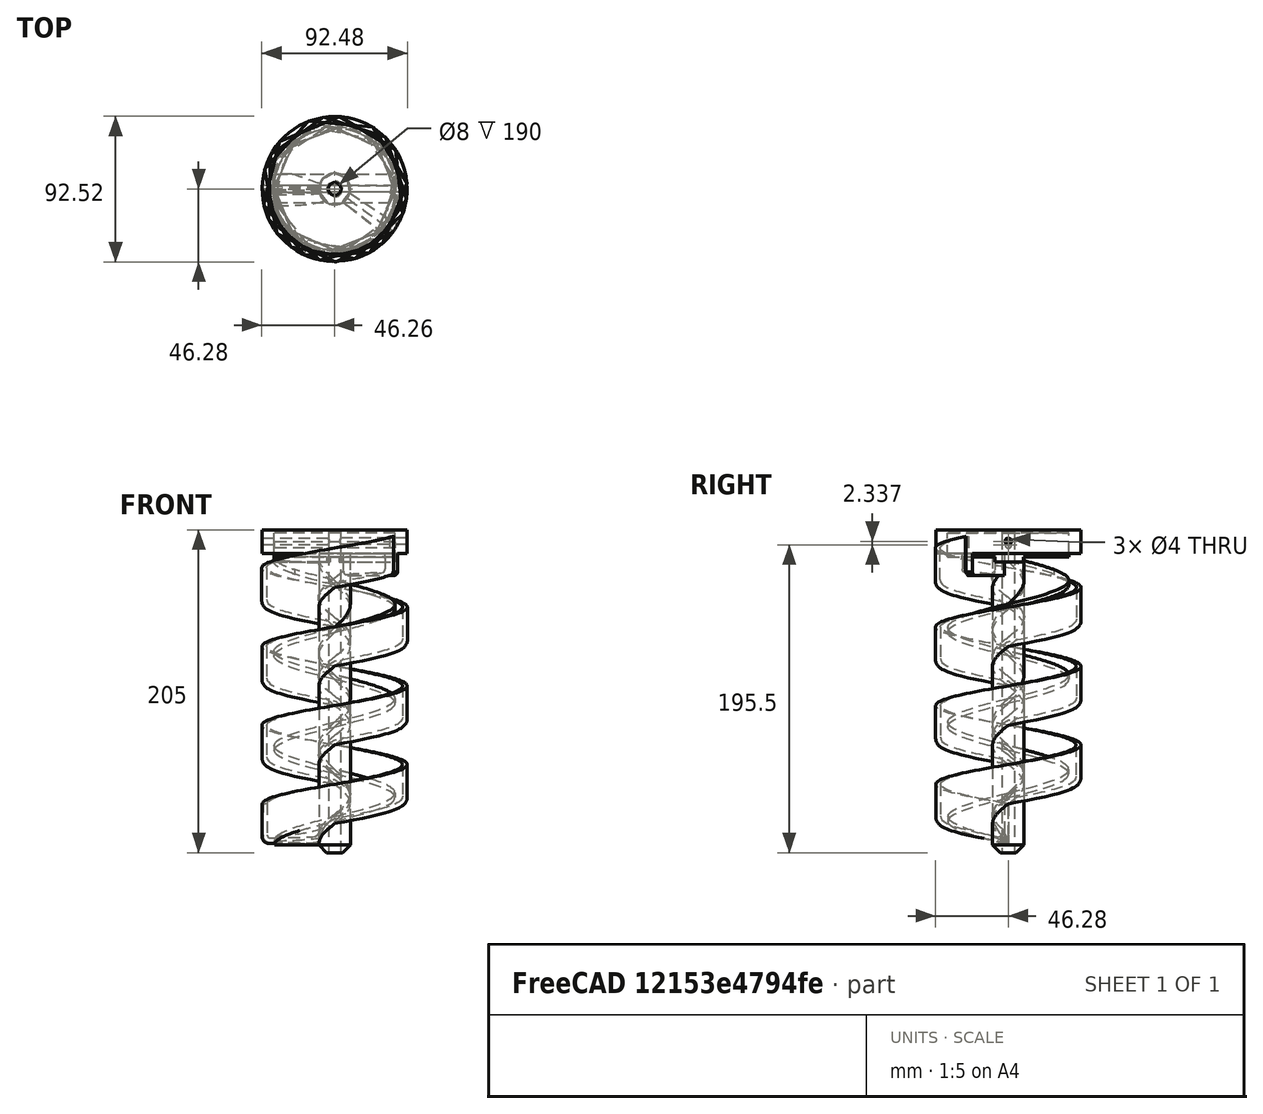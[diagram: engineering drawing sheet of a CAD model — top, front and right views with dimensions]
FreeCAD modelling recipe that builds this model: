
FCSTD DOCUMENT  (FreeCAD 1.1R14555 (Git shallow))
Label: Body - 1.2
License: All rights reserved
LicenseURL: https://en.wikipedia.org/wiki/All_rights_reserved
objects: Sketcher::SketchObject×14, PartDesign::Pad×8, PartDesign::Pocket×7, PartDesign::Chamfer×6, PartDesign::AdditiveHelix×2, PartDesign::Body×2, App::Point×2, PartDesign::Fillet×1
note: 102 computed .brp shape members not serialized (recipe doc carries the construction recipe); baked Part::Feature solids carry a one-line shape summary decoded from their .brp

FEATURE [Sketcher::SketchObject] Sketch
  ArcFitTolerance = 1e-06
  AttachmentSupport = -> [XY_Plane]
  ExternalTypes = [0]
  FullyConstrained = true
  MakeInternals = false
  MapMode = 5
  sketch-geometry (1):
    g0: Circle CenterX=0 CenterY=0 CenterZ=0 NormalX=0 NormalY=0 NormalZ=1 AngleXU=0 Radius=10
  constraints (2):
    c: Coincident(g0,g-1)
    c: Diameter(g0) = 20
FEATURE [PartDesign::Pad] Pad
  Direction = (0,0,1)
  Length = 200
  Length2 = 10
  Profile = -> Sketch
  ReferenceAxis = -> Sketch [N_Axis]
  Refine = true
  SideType = 0
  Suppressed = false
  Type = 0
  Type2 = 0
FEATURE [PartDesign::Chamfer] Chamfer
  Angle = 45
  Base = -> Pad [Edge2]
  BaseFeature = -> Pad
  ChamferType = 0
  FlipDirection = false
  Refine = true
  Size = 5
  Size2 = 1
  SupportTransform = false
  Suppressed = false
  UseAllEdges = false
FEATURE [Sketcher::SketchObject] Sketch001
  ArcFitTolerance = 1e-06
  AttachmentSupport = -> [XZ_Plane]
  ExternalGeometry = -> [Chamfer]
  ExternalTypes = [0]
  FullyConstrained = true
  MakeInternals = false
  MapMode = 5
  Placement = pos=(0,0,0) rot=(1,0,0;1.5708rad)
  expr: Constraints[11] = 77 / 2 - 0.3
  sketch-geometry (4):
    g0: LineSegment StartX=-38.2 StartY=8 StartZ=0 EndX=-38.2 EndY=5 EndZ=0
    g1: LineSegment StartX=-38.2 StartY=5 StartZ=0 EndX=0 EndY=5 EndZ=0
    g2: LineSegment StartX=0 StartY=5 StartZ=0 EndX=0 EndY=8 EndZ=0
    g3: LineSegment StartX=0 StartY=8 StartZ=0 EndX=-38.2 EndY=8 EndZ=0
  constraints (12):
    c: Coincident(g0,g1)
    c: Coincident(g1,g2)
    c: Coincident(g2,g3)
    c: Coincident(g3,g0)
    c: Vertical(g0)
    c: Vertical(g2)
    c: Horizontal(g1)
    c: Horizontal(g3)
    c: PointOnObject(g1,g-2)
    c: Horizontal(g0,g-3)
    c: DistanceY(g0,g0) = 3
    c: DistanceX(g1,g1) = 38.2
FEATURE [PartDesign::AdditiveHelix] AdditiveHelix
  Angle = 0.1
  Axis = (0,2e-16,1)
  Base = (0,0,0)
  BaseFeature = -> Chamfer
  Growth = 0.10472
  HasBeenEdited = true
  Height = 180
  LeftHanded = false
  Mode = 0
  Outside = false
  Pitch = 60
  Profile = -> Sketch001
  ReferenceAxis = -> Sketch001 [V_Axis]
  Refine = true
  Suppressed = false
  Tolerance = 0.1
  Turns = 3
FEATURE [Sketcher::SketchObject] Sketch002
  ArcFitTolerance = 1e-06
  AttachmentSupport = -> [Chamfer]
  ExternalTypes = [0]
  FullyConstrained = true
  MakeInternals = false
  MapMode = 5
  Placement = pos=(0,0,200) rot=(0,0,1;0rad)
  sketch-geometry (1):
    g0: Circle CenterX=0 CenterY=0 CenterZ=0 NormalX=0 NormalY=0 NormalZ=1 AngleXU=0 Radius=38.5
  constraints (2):
    c: Coincident(g0,g-1)
    c: Diameter(g0) = 77
FEATURE [PartDesign::Chamfer] Chamfer001
  Angle = 45
  Base = -> AdditiveHelix [Edge12]
  BaseFeature = -> AdditiveHelix
  ChamferType = 0
  FlipDirection = false
  Refine = true
  Size = 2.99
  Size2 = 1
  SupportTransform = false
  Suppressed = false
  UseAllEdges = false
FEATURE [PartDesign::Chamfer] Chamfer002
  Angle = 45
  Base = -> Chamfer001 [Edge12]
  BaseFeature = -> Chamfer001
  ChamferType = 0
  FlipDirection = false
  Refine = true
  Size = 4
  Size2 = 1
  SupportTransform = false
  Suppressed = false
  UseAllEdges = false
FEATURE [PartDesign::Chamfer] Chamfer003
  Angle = 45
  Base = -> Chamfer002 [Edge13]
  BaseFeature = -> Chamfer002
  ChamferType = 0
  FlipDirection = false
  Refine = true
  Size = 4
  Size2 = 1
  SupportTransform = false
  Suppressed = false
  UseAllEdges = false
FEATURE [PartDesign::Pad] Pad001
  BaseFeature = -> Chamfer003
  Direction = (0,0,1)
  Length = 3
  Length2 = 10
  Profile = -> Sketch002
  ReferenceAxis = -> Sketch002 [N_Axis]
  Refine = true
  SideType = 0
  Suppressed = false
  Type = 0
  Type2 = 0
FEATURE [Sketcher::SketchObject] Sketch003
  ArcFitTolerance = 1e-06
  AttachmentSupport = -> [Pad001]
  ExternalTypes = [0]
  FullyConstrained = true
  MakeInternals = false
  MapMode = 5
  Placement = pos=(0,0,200) rot=(1,0,0;3.14159rad)
  sketch-geometry (1):
    g0: Circle CenterX=0 CenterY=0 CenterZ=0 NormalX=0 NormalY=0 NormalZ=1 AngleXU=0 Radius=38.5
  constraints (2):
    c: Coincident(g0,g-1)
    c: Diameter(g0) = 77
FEATURE [PartDesign::Pad] Pad002
  BaseFeature = -> Pad001
  Direction = (0,0,-1)
  Length = 12
  Length2 = 10
  Profile = -> Sketch003
  ReferenceAxis = -> Sketch003 [N_Axis]
  Refine = true
  SideType = 0
  Suppressed = false
  Type = 0
  Type2 = 0
FEATURE [PartDesign::Fillet] Fillet
  Base = -> Pad002 [Edge36]
  BaseFeature = -> Pad002
  Radius = 3
  Refine = true
  SupportTransform = false
  Suppressed = false
  UseAllEdges = false
FEATURE [Sketcher::SketchObject] Sketch004
  ArcFitTolerance = 1e-06
  AttachmentSupport = -> [Fillet]
  ExternalTypes = [0]
  FullyConstrained = true
  MakeInternals = false
  MapMode = 5
  Placement = pos=(0,0,203) rot=(0,0,1;0rad)
  sketch-geometry (2):
    g0: Circle CenterX=0 CenterY=0 CenterZ=0 NormalX=0 NormalY=0 NormalZ=1 AngleXU=0 Radius=38.5
    g1: Circle CenterX=0 CenterY=0 CenterZ=0 NormalX=0 NormalY=0 NormalZ=1 AngleXU=0 Radius=50
  constraints (4):
    c: Coincident(g0,g-1)
    c: Diameter(g0) = 77
    c: Coincident(g1,g0)
    c: Diameter(g1) = 100
FEATURE [PartDesign::Pocket] Pocket
  BaseFeature = -> Fillet
  Direction = (0,0,-1)
  Length = 180
  Length2 = 5
  Profile = -> Sketch004
  ReferenceAxis = -> Sketch004 [N_Axis]
  Refine = true
  Reversed = true
  SideType = 0
  Suppressed = false
  Type = 0
  Type2 = 0
FEATURE [Sketcher::SketchObject] Sketch005
  ArcFitTolerance = 1e-06
  AttachmentSupport = -> [YZ_Plane]
  ExternalGeometry = -> [Pocket]
  ExternalTypes = [0]
  FullyConstrained = true
  MakeInternals = false
  MapMode = 5
  Placement = pos=(0,0,0) rot=(0.57735,0.57735,0.57735;2.0944rad)
  sketch-geometry (1):
    g0: Circle CenterX=9.4e-15 CenterY=195.5 CenterZ=0 NormalX=0 NormalY=0 NormalZ=1 AngleXU=0 Radius=2
  constraints (3):
    c: PointOnObject(g0,g-3)
    c: Diameter(g0) = 4
    c: Symmetric(g-3,g-3,g0)
FEATURE [PartDesign::Pocket] Pocket001
  BaseFeature = -> Pocket
  Direction = (-1,0,0)
  Length = 500
  Length2 = 5
  Profile = -> Sketch005
  ReferenceAxis = -> Sketch005 [N_Axis]
  Refine = true
  Reversed = true
  SideType = 0
  Suppressed = false
  Type = 0
  Type2 = 0
FEATURE [PartDesign::Pocket] Pocket002
  BaseFeature = -> Pocket001
  Direction = (-1,0,0)
  Length = 5
  Length2 = 5
  Profile = -> Pocket001 [Face21]
  Refine = true
  SideType = 0
  Suppressed = false
  Type = 1
  Type2 = 0
FEATURE [Sketcher::SketchObject] Sketch006
  ArcFitTolerance = 1e-06
  AttachmentSupport = -> [YZ_Plane]
  ExternalTypes = [0]
  FullyConstrained = false
  MakeInternals = false
  MapMode = 5
  Placement = pos=(0,0,0) rot=(0.57735,0.57735,0.57735;2.0944rad)
  sketch-geometry (4):
    g0: LineSegment StartX=9.56195 StartY=192.563 StartZ=0 EndX=-8.62475 EndY=192.563 EndZ=0
    g1: LineSegment StartX=-8.62475 StartY=192.563 StartZ=0 EndX=-8.62475 EndY=184.759 EndZ=0
    g2: LineSegment StartX=-8.62475 StartY=184.759 StartZ=0 EndX=9.56195 EndY=184.759 EndZ=0
    g3: LineSegment StartX=9.56195 StartY=184.759 StartZ=0 EndX=9.56195 EndY=192.563 EndZ=0
  constraints (8):
    c: Coincident(g0,g1)
    c: Coincident(g1,g2)
    c: Coincident(g2,g3)
    c: Coincident(g3,g0)
    c: Horizontal(g0)
    c: Horizontal(g2)
    c: Vertical(g1)
    c: Vertical(g3)
FEATURE [PartDesign::Pad] Pad003
  BaseFeature = -> Pocket002
  Direction = (1,0,0)
  Length = 50
  Length2 = 50
  Profile = -> Sketch006
  ReferenceAxis = -> Sketch006 [N_Axis]
  Refine = true
  SideType = 0
  Suppressed = false
  Type = 4
  Type2 = 0
FEATURE [Sketcher::SketchObject] Sketch007
  ArcFitTolerance = 1e-06
  AttachmentSupport = -> [Pad003]
  ExternalTypes = [0]
  FullyConstrained = true
  MakeInternals = false
  MapMode = 5
  Placement = pos=(0,0,203) rot=(0,0,1;0rad)
  sketch-geometry (2):
    g0: Circle CenterX=0 CenterY=0 CenterZ=0 NormalX=0 NormalY=0 NormalZ=1 AngleXU=0 Radius=38.5
    g1: Circle CenterX=0 CenterY=0 CenterZ=0 NormalX=0 NormalY=0 NormalZ=1 AngleXU=0 Radius=55
  constraints (4):
    c: Coincident(g0,g-1)
    c: Diameter(g0) = 77
    c: Diameter(g1) = 110
    c: Coincident(g1,g0)
FEATURE [PartDesign::Pocket] Pocket003
  BaseFeature = -> Pad003
  Direction = (0,0,-1)
  Length = 30
  Length2 = 5
  Profile = -> Sketch007
  ReferenceAxis = -> Sketch007 [N_Axis]
  Refine = true
  SideType = 0
  Suppressed = false
  Type = 0
  Type2 = 0
FEATURE [PartDesign::Body] Body
  AllowCompound = false
  Group = -> [Sketch,Pad,Chamfer,Sketch001,AdditiveHelix,Sketch002,Chamfer001,Chamfer002,Chamfer003,Pad001,Sketch003,Pad002,Fillet,Sketch004,Pocket,Sketch005,Pocket001,Pocket002,Sketch006,Pad003,Sketch007,Pocket003]
  Origin = -> Origin
  Tip = -> Pocket003
FEATURE [Sketcher::SketchObject] Sketch008
  ArcFitTolerance = 1e-06
  AttachmentSupport = -> [XY_Plane001]
  ExternalTypes = [0]
  FullyConstrained = true
  MakeInternals = false
  MapMode = 5
  sketch-geometry (2):
    g0: Circle CenterX=0 CenterY=0 CenterZ=0 NormalX=0 NormalY=0 NormalZ=1 AngleXU=0 Radius=10
    g1: Circle CenterX=0 CenterY=0 CenterZ=0 NormalX=0 NormalY=0 NormalZ=1 AngleXU=0 Radius=4
  constraints (4):
    c: Coincident(g0,g-1)
    c: Diameter(g0) = 20
    c: Coincident(g1,g0)
    c: Diameter(g1) = 8
FEATURE [PartDesign::Pad] Pad004
  Direction = (0,0,1)
  Length = 200
  Length2 = 10
  Profile = -> Sketch008
  ReferenceAxis = -> Sketch008 [N_Axis]
  Refine = true
  SideType = 0
  Suppressed = false
  Type = 0
  Type2 = 0
FEATURE [PartDesign::Chamfer] Chamfer004
  Angle = 45
  Base = -> Pad004 [Edge2]
  BaseFeature = -> Pad004
  ChamferType = 0
  FlipDirection = false
  Refine = true
  Size = 5
  Size2 = 1
  SupportTransform = false
  Suppressed = false
  UseAllEdges = false
FEATURE [Sketcher::SketchObject] Sketch009
  ArcFitTolerance = 1e-06
  AttachmentSupport = -> [XZ_Plane001]
  ExternalGeometry = -> [Chamfer004]
  ExternalTypes = [0]
  FullyConstrained = true
  MakeInternals = false
  MapMode = 5
  Placement = pos=(0,0,0) rot=(1,0,0;1.5708rad)
  sketch-geometry (12):
    g0: LineSegment StartX=-42 StartY=6 StartZ=0 EndX=-10 EndY=6 EndZ=0
    g1: LineSegment StartX=-13 StartY=9 StartZ=0 EndX=-41 EndY=9 EndZ=0
    g2: LineSegment StartX=-46 StartY=10 StartZ=0 EndX=-46 EndY=31 EndZ=0
    g3: LineSegment StartX=-43 StartY=31 StartZ=0 EndX=-43 EndY=11 EndZ=0
    g4: ArcOfCircle CenterX=-41 CenterY=11 CenterZ=0 NormalX=0 NormalY=0 NormalZ=1 AngleXU=0 Radius=2 StartAngle=3.14159 EndAngle=4.71239
    g5: GeomPoint [constr] X=-43 Y=9 Z=0
    g6: ArcOfCircle CenterX=-42 CenterY=10 CenterZ=0 NormalX=0 NormalY=0 NormalZ=1 AngleXU=0 Radius=4 StartAngle=3.14159 EndAngle=4.71239
    g7: ArcOfCircle CenterX=-13 CenterY=12 CenterZ=0 NormalX=0 NormalY=0 NormalZ=1 AngleXU=0 Radius=3 StartAngle=4.71239 EndAngle=6.28319
    g8: LineSegment StartX=-10 StartY=12 StartZ=0 EndX=-8 EndY=12 EndZ=0
    g9: LineSegment StartX=-10 StartY=6 StartZ=0 EndX=-8 EndY=6 EndZ=0
    g10: LineSegment StartX=-8 StartY=12 StartZ=0 EndX=-8 EndY=6 EndZ=0
    g11: LineSegment StartX=-46 StartY=31 StartZ=0 EndX=-43 EndY=31 EndZ=0
  constraints (34):
    c: Vertical(g2)
    c: Vertical(g3)
    c: PointOnObject(g5,g1)
    c: PointOnObject(g5,g3)
    c: Tangent(g1,g4) = 1.5708
    c: Tangent(g3,g4) = -1.5708
    c: Tangent(g0,g6) = -1.5708
    c: Tangent(g2,g6) = 1.5708
    c: DistanceY(g3,g3) = 20
    c: Radius(g4) = 2
    c: Radius(g6) = 4
    c: Horizontal(g1)
    c: Horizontal(g0)
    c: Vertical(g0,g-3)
    c: DistanceX(g2,g-1) = 46
    c: DistanceY(g-1,g0) = 6
    c: Coincident(g7,g1)
    c: Vertical(g7,g1)
    c: Radius(g7) = 3
    c: Vertical(g7,g0)
    c: Horizontal(g7,g7)
    c: DistanceY(g0,g1) = 3
    c: Coincident(g8,g7)
    c: Coincident(g9,g0)
    c: Horizontal(g9)
    c: Coincident(g10,g8)
    c: Coincident(g10,g9)
    c: Vertical(g10)
    c: Horizontal(g8)
    c: Distance(g8,g8) = 2
    c: Horizontal(g2,g3)
    c: DistanceX(g2,g3) = 3
    c: Coincident(g11,g2)
    c: Coincident(g11,g3)
FEATURE [PartDesign::AdditiveHelix] AdditiveHelix001
  Angle = 0.1
  Axis = (0,2e-16,1)
  Base = (0,0,0)
  BaseFeature = -> Chamfer004
  Growth = 0.0872666
  HasBeenEdited = true
  Height = 170
  LeftHanded = false
  Mode = 0
  Outside = false
  Pitch = 50
  Profile = -> Sketch009
  ReferenceAxis = -> Sketch009 [V_Axis]
  Refine = true
  Suppressed = false
  Tolerance = 0.1
  Turns = 3.4
FEATURE [App::Point] Origin002  label="Origin"
  Role = Origin
FEATURE [App::Point] Origin003  label="Origin"
  Role = Origin
FEATURE [Sketcher::SketchObject] Sketch010
  ArcFitTolerance = 1e-06
  AttachmentSupport = -> [AdditiveHelix001]
  ExternalTypes = [0]
  FullyConstrained = true
  MakeInternals = false
  MapMode = 5
  Placement = pos=(0,0,200) rot=(0,0,1;0rad)
  expr: Constraints[3] = 46 * 2
  sketch-geometry (2):
    g0: Circle CenterX=0 CenterY=0 CenterZ=0 NormalX=0 NormalY=0 NormalZ=1 AngleXU=0 Radius=4
    g1: Circle CenterX=0 CenterY=0 CenterZ=0 NormalX=0 NormalY=0 NormalZ=1 AngleXU=0 Radius=46
  constraints (4):
    c: Diameter(g0) = 8
    c: Coincident(g0,g-1)
    c: Coincident(g1,g0)
    c: Diameter(g1) = 92
FEATURE [PartDesign::Pad] Pad005
  BaseFeature = -> AdditiveHelix001
  Direction = (0,0,1)
  Length = 5
  Length2 = 10
  Profile = -> Sketch010
  ReferenceAxis = -> Sketch010 [N_Axis]
  SideType = 1
  Suppressed = false
  Type = 0
  Type2 = 0
FEATURE [Sketcher::SketchObject] Sketch011
  ArcFitTolerance = 1e-06
  AttachmentSupport = -> [Pad005]
  ExternalTypes = [0]
  FullyConstrained = false
  MakeInternals = false
  MapMode = 5
  Placement = pos=(0,0,205) rot=(0,0,1;0rad)
  sketch-geometry (4):
    g0: LineSegment StartX=3.72918 StartY=1.44679 StartZ=0 EndX=40.0304 EndY=-22.662 EndZ=0
    g1: LineSegment StartX=34.1872 StartY=-30.7772 StartZ=0 EndX=-0.528085 EndY=-3.96499 EndZ=0
    g2: ArcOfCircle CenterX=0 CenterY=0 CenterZ=0 NormalX=0 NormalY=0 NormalZ=1 AngleXU=0 Radius=46 StartAngle=5.55023 EndAngle=5.76805
    g3: ArcOfCircle CenterX=0 CenterY=0 CenterZ=0 NormalX=0 NormalY=0 NormalZ=1 AngleXU=0 Radius=4 StartAngle=4.57998 EndAngle=6.65327
  constraints (9):
    c: Distance(g0,g1) = 10
    c: Coincident(g2,g-1)
    c: Coincident(g3,g2)
    c: Radius(g3) = 4
    c: Coincident(g3,g1)
    c: Coincident(g3,g0)
    c: Coincident(g2,g0)
    c: Coincident(g1,g2)
    c: Radius(g2) = 46
FEATURE [PartDesign::Pad] Pad006
  BaseFeature = -> Pad005
  Direction = (0,0,1)
  Length = 18
  Length2 = 10
  Profile = -> Sketch011
  ReferenceAxis = -> Sketch011 [N_Axis]
  Reversed = true
  SideType = 0
  Suppressed = false
  Type = 0
  Type2 = 0
FEATURE [PartDesign::Pad] Pad007
  BaseFeature = -> Pad006
  Direction = (0,0,-1)
  Length = 14
  Length2 = 10
  Profile = -> Pad006 [Face29]
  SideType = 0
  Suppressed = false
  Type = 0
  Type2 = 0
FEATURE [PartDesign::Pocket] Pocket004
  BaseFeature = -> Pad007
  Direction = (0.59,0.81,0)
  Length = 15
  Length2 = 5
  Profile = -> Pad007 [Face23]
  SideType = 0
  Suppressed = false
  Type = 0
  Type2 = 0
FEATURE [Sketcher::SketchObject] Sketch012
  ArcFitTolerance = 1e-06
  AttachmentSupport = -> [Origin001]
  ExternalTypes = [0]
  FullyConstrained = false
  MakeInternals = false
  MapMode = 5
  Placement = pos=(0,0,0) rot=(0.57735,0.57735,0.57735;2.0944rad)
  sketch-geometry (1):
    g0: Circle CenterX=0 CenterY=197.837 CenterZ=0 NormalX=0 NormalY=0 NormalZ=1 AngleXU=0 Radius=2
  constraints (2):
    c: PointOnObject(g0,g-2)
    c: Diameter(g0) = 4
FEATURE [PartDesign::Pocket] Pocket005
  BaseFeature = -> Pocket004
  Direction = (-1,0,0)
  Length = 60
  Length2 = 60
  Profile = -> Sketch012
  ReferenceAxis = -> Sketch012 [N_Axis]
  SideType = 1
  Suppressed = false
  Type = 0
  Type2 = 0
FEATURE [Sketcher::SketchObject] Sketch013
  ArcFitTolerance = 1e-06
  AttachmentSupport = -> [Pocket005]
  ExternalTypes = [0]
  FullyConstrained = false
  MakeInternals = false
  MapMode = 5
  Placement = pos=(0,0,205) rot=(0,0,1;0rad)
  expr: Constraints[2] = 2 * 46
  sketch-geometry (2):
    g0: Circle CenterX=0 CenterY=0 CenterZ=0 NormalX=0 NormalY=0 NormalZ=1 AngleXU=0 Radius=46
    g1: Circle CenterX=0 CenterY=0 CenterZ=0 NormalX=0 NormalY=0 NormalZ=1 AngleXU=0 Radius=61.8389
  constraints (3):
    c: Coincident(g0,g-1)
    c: Coincident(g1,g0)
    c: Diameter(g0) = 92
FEATURE [PartDesign::Pocket] Pocket006
  BaseFeature = -> Pocket005
  Direction = (0,0,-1)
  Length = 250
  Length2 = 5
  Profile = -> Sketch013
  ReferenceAxis = -> Sketch013 [N_Axis]
  SideType = 0
  Suppressed = false
  Type = 0
  Type2 = 0
FEATURE [PartDesign::Chamfer] Chamfer005
  Angle = 45
  Base = -> Pocket006 [Edge15]
  BaseFeature = -> Pocket006
  ChamferType = 0
  FlipDirection = false
  Size = 2.5
  Size2 = 1
  SupportTransform = false
  Suppressed = false
  UseAllEdges = false
FEATURE [PartDesign::Body] Body001
  AllowCompound = false
  Group = -> [Sketch008,Pad004,Chamfer004,Sketch009,AdditiveHelix001,Sketch010,Pad005,Sketch011,Pad006,Pad007,Pocket004,Sketch012,Pocket005,Sketch013,Pocket006,Chamfer005]
  Origin = -> Origin001
  Tip = -> Chamfer005
